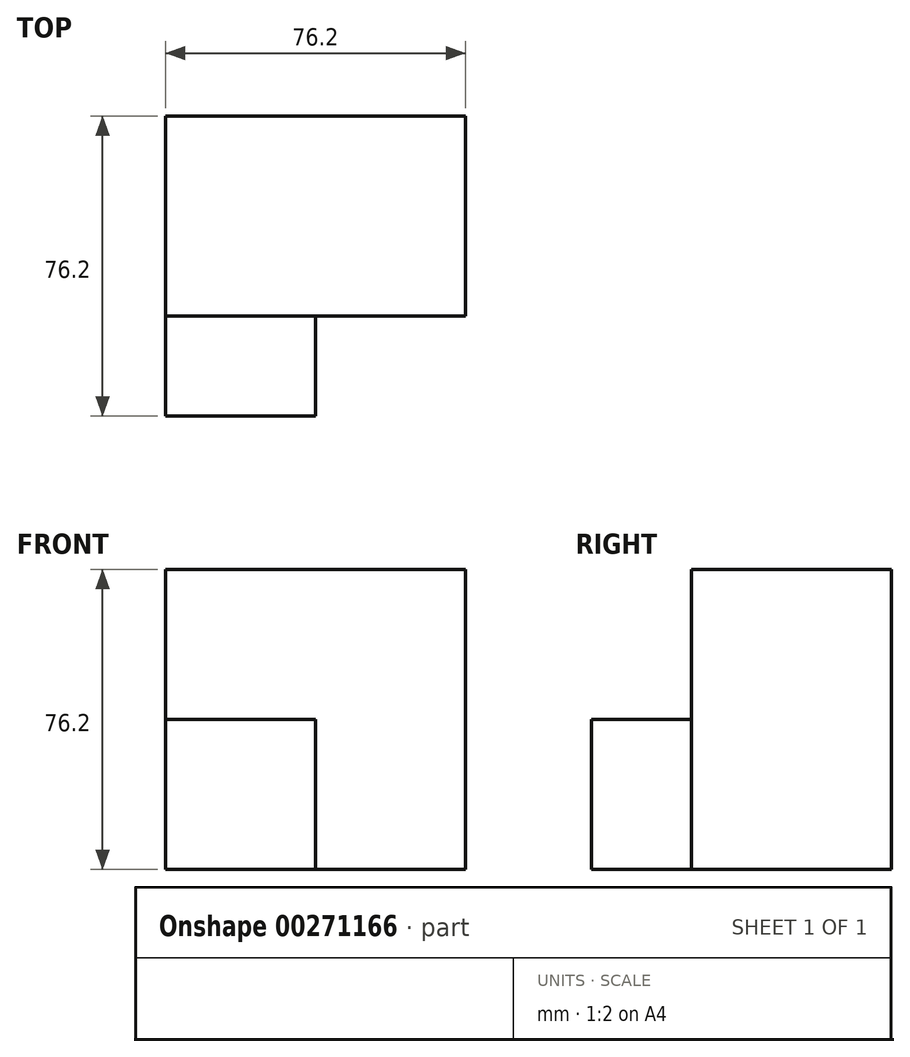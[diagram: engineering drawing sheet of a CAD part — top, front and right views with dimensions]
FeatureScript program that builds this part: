
annotation { "Feature Type Name" : "Feature", "Feature Type Description" : "" }
export const myFeature = defineFeature(function(context is Context, id is Id, definition is map)
    precondition{}
    {
        {
            var Q0;
            Q0=qCreatedBy(makeId("Front.planeOp"),FACE);
            var sketch = newSketch(context, id + "F0", { "sketchPlane" : qUnion([Q0])});
            skLineSegment(sketch, "E0.bottom", {"start": v(0, 0) * mm, "end": v(-76.2, 0) * mm});
            skLineSegment(sketch, "E0.top", {"start": v(0, 76.2) * mm, "end": v(-76.2, 76.2) * mm});
            skLineSegment(sketch, "E0.left", {"start": v(0, 0) * mm, "end": v(0, 76.2) * mm});
            skLineSegment(sketch, "E0.right", {"start": v(-76.2, 0) * mm, "end": v(-76.2, 76.2) * mm});
            skSolve(sketch);
        }
        {
            var Q0;
            Q0=makeQuery(id+"F0.imprint","IMPRINT",FACE,{"disambiguationData":[TD([[makeQuery(id+"F0.imprint","IMPRINT",EDGE,{"derivedFrom":sQuery(id+"F0.wireOp",EDGE,"E0.bottom")}),-1.0]])]});
            var sketch = newSketch(context, id + "F1", { "sketchPlane" : qUnion([Q0])});
            skSolve(sketch);
        }
        {
            var Q0;
            Q0=makeQuery(id+"F1.imprint","IMPRINT",FACE,{"disambiguationData":[TD([[makeQuery(id+"F1.imprint","IMPRINT",EDGE,{"derivedFrom":makeQuery(id+"F0.imprint","IMPRINT",EDGE,{"derivedFrom":sQuery(id+"F0.wireOp",EDGE,"E0.bottom")})}),-1.0]])]});
            extrude(context, id + "F2", {"entities" : qUnion([Q0]), "depth" : 50.8 * mm});
        }
        {
            var Q0;
            Q0=makeQuery(id+"F2.opExtrude","CAP_FACE",FACE,{"disambiguationData":[OSD([sQuery(id+"F0.wireOp",EDGE,"E0.bottom"),sQuery(id+"F0.wireOp",EDGE,"E0.top"),sQuery(id+"F0.wireOp",EDGE,"E0.left"),sQuery(id+"F0.wireOp",EDGE,"E0.right")])],"isStart":false});
            var sketch = newSketch(context, id + "F3", { "sketchPlane" : qUnion([Q0])});
            skLineSegment(sketch, "E1", {"start": v(-76.2, 0) * mm, "end": v(-38.1, 0) * mm});
            skLineSegment(sketch, "E2", {"start": v(-38.1, 0) * mm, "end": v(-38.1, 38.1) * mm});
            skLineSegment(sketch, "E3", {"start": v(-38.1, 38.1) * mm, "end": v(-76.2, 38.1) * mm});
            skLineSegment(sketch, "E4", {"start": v(-76.2, 38.1) * mm, "end": v(-76.2, 0) * mm});
            skSolve(sketch);
        }
        {
            var Q0;
            Q0=makeQuery(id+"F3.imprint","IMPRINT",FACE,{"disambiguationData":[TD([[makeQuery(id+"F3.imprint","IMPRINT",EDGE,{"derivedFrom":sQuery(id+"F3.wireOp",EDGE,"E1")}),-1.0]])]});
            extrude(context, id + "F4", {"entities" : qUnion([Q0]), "operationType" : NewBodyOperationType.ADD, "depth" : 25.4 * mm});
        }
    });
